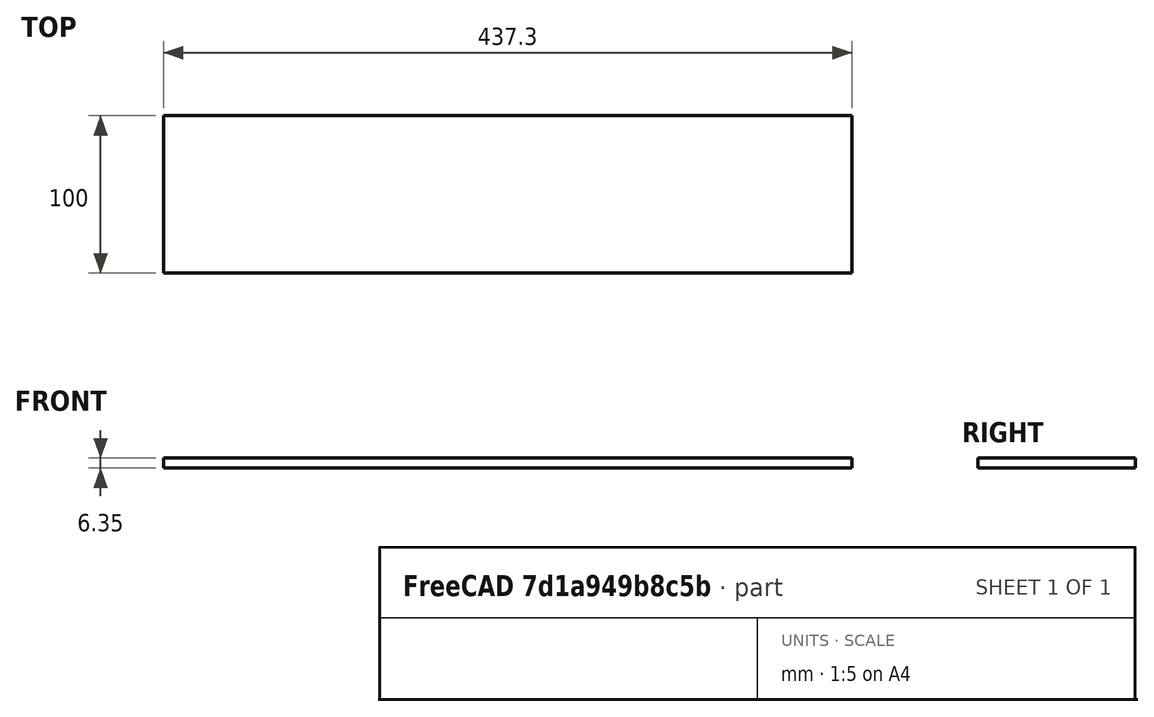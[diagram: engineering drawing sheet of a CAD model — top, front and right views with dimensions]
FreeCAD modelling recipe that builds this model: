
FCSTD DOCUMENT  (FreeCAD 0.16RUnknown)
Label: Frontal
License: All rights reserved
LicenseURL: http://berserk.design
objects: Sketcher::SketchObject×1, PartDesign::Pad×1
note: 3 computed .brp shape members not serialized (recipe doc carries the construction recipe); baked Part::Feature solids carry a one-line shape summary decoded from their .brp

FEATURE [Sketcher::SketchObject] Sketch
  sketch-geometry (4):
    g0: LineSegment StartX=0 StartY=0 StartZ=0 EndX=437.3 EndY=0 EndZ=0
    g1: LineSegment StartX=437.3 StartY=0 StartZ=0 EndX=437.3 EndY=100 EndZ=0
    g2: LineSegment StartX=437.3 StartY=100 StartZ=0 EndX=0 EndY=100 EndZ=0
    g3: LineSegment StartX=0 StartY=100 StartZ=0 EndX=0 EndY=0 EndZ=0
  constraints (11):
    c: Coincident(g0,g1)
    c: Coincident(g1,g2)
    c: Coincident(g2,g3)
    c: Coincident(g3,g0)
    c: Horizontal(g0)
    c: Horizontal(g2)
    c: Vertical(g1)
    c: Vertical(g3)
    c: Coincident(g0,g-1)
    c: DistanceY(g3,g3) = 100
    c: DistanceX(g2,g2) = 437.3
FEATURE [PartDesign::Pad] Pad
  Length = 6.35
  Length2 = 100
  Sketch = -> Sketch
  Type = 0
